# Revit family: 3352SB-15-HQ
name_source: partatom
category: Plumbing Fixtures
revit_build: Autodesk Revit Architecture 2012 (Build: 20110309_2315(x64)
units: mm (PartAtom-declared; Revit-internal decimal feet)

## types (1)
- 3352SB-15-HQ
    1/2" light pattern tap washer = C-098-15
    Assembly Code = D2010
    CW Connection = Yes
    CWFU = 0
    Connection backnut = 088-15
    Cost = 0 $
    Default Elevation = 0' - 0"
    Description = Pillar type with diverter and handshower attachment. 1/2"BSP male inlet
    HW Connection = Yes
    HWFU = 0
    Handshower = E-007/2
    Handshower hose = 008/4C
    Headpart complete = P-61-1SB
    Keynote = Wall mounted handshower holder
    Manufacturer = COBRA
    Material = Chrome - Polished
    Model = 3352SB-15-HQ
    Pair of handles = C-HA-ST BR
    Range = Stella Bright
    Type Comments = SANS 226 TYPE 2
    URL = http://www.cobra.co.za
    Vent Connection = No
    WFU = 0
    Wall mounted handshower holder = 28020
    Waste Connection = No

## geometry (parser evidence)
native form markers: Blend x5
no freeform markers — native parametric forms only
